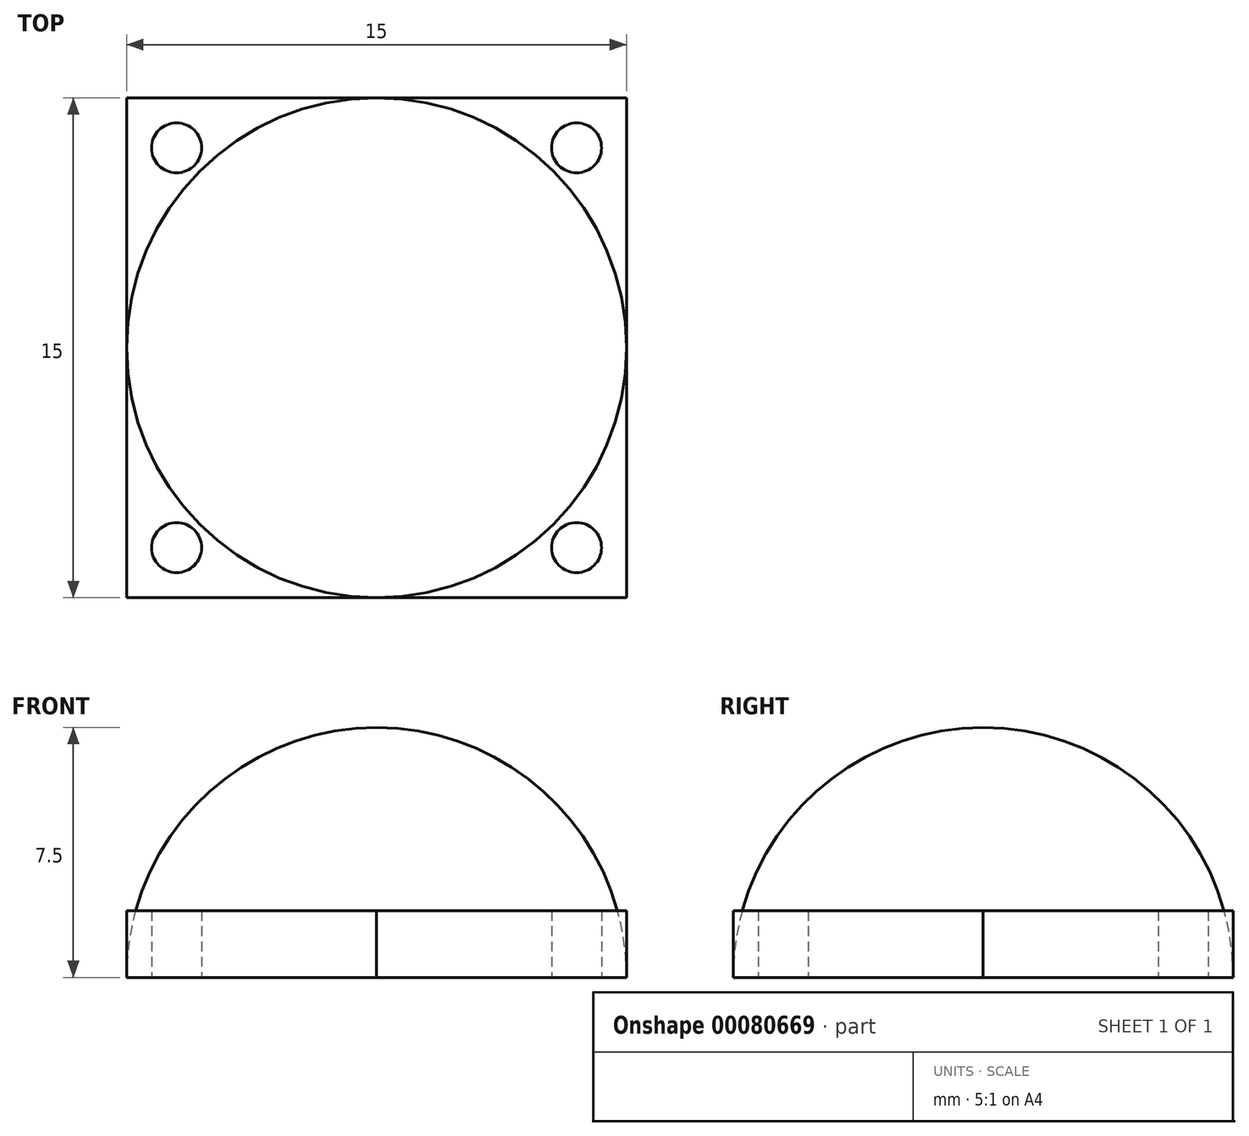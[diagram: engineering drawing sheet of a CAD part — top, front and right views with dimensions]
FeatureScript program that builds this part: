
annotation { "Feature Type Name" : "Feature", "Feature Type Description" : "" }
export const myFeature = defineFeature(function(context is Context, id is Id, definition is map)
    precondition{}
    {
        {
            var Q0;
            Q0=qCreatedBy(makeId("Top.planeOp"),FACE);
            var sketch = newSketch(context, id + "F0", { "sketchPlane" : qUnion([Q0])});
            skLineSegment(sketch, "E0.bottom", {"start": v(7.5, -7.5) * mm, "end": v(-7.5, -7.5) * mm});
            skLineSegment(sketch, "E0.top", {"start": v(7.5, 7.5) * mm, "end": v(-7.5, 7.5) * mm});
            skLineSegment(sketch, "E0.left", {"start": v(7.5, -7.5) * mm, "end": v(7.5, 7.5) * mm});
            skLineSegment(sketch, "E0.right", {"start": v(-7.5, -7.5) * mm, "end": v(-7.5, 7.5) * mm});
            skPoint(sketch, "E0.middle", {"position": v(0, 0) * mm});
            skCircle(sketch, "E1", {"center": v(0, 0) * mm, "radius": 7.5 * mm});
            skLineSegment(sketch, "E2", {"start": v(0, 0) * mm, "end": v(7.5, 0) * mm, "construction": true});
            skLineSegment(sketch, "E3", {"start": v(0, 7.5) * mm, "end": v(0, -7.5) * mm});
            skCircle(sketch, "E4", {"center": v(-6, 6) * mm, "radius": 0.75 * mm});
            skCircle(sketch, "E5.1.0", {"center": v(-6, -6) * mm, "radius": 0.75 * mm});
            skCircle(sketch, "E5.2.0", {"center": v(6, -6) * mm, "radius": 0.75 * mm});
            skCircle(sketch, "E5.3.0", {"center": v(6, 6) * mm, "radius": 0.75 * mm});
            skSolve(sketch);
        }
        {
            var Q0;
            {var subQ0=sQuery(id+"F0.wireOp",EDGE,"E3");Q0=makeQuery(id+"F0.imprint","IMPRINT",FACE,{"disambiguationData":[TD([[makeQuery(id+"F0.imprint","IMPRINT",EDGE,{"derivedFrom":subQ0}),-1.0]])]});}
            var Q1;
            Q1=sQuery(id+"F0.wireOp",EDGE,"E3");
            revolve(context, id + "F1", {"entities" : qUnion([Q0]), "axis" : qUnion([Q1]), "revolveType" : RevolveType.ONE_DIRECTION, "oppositeDirection" : true, "angle" : 180 * degree});
        }
        {
            var Q0;
            {var subQ0=sQuery(id+"F0.wireOp",EDGE,"E0.right");var subQ1=sQuery(id+"F0.wireOp",EDGE,"E0.top");var subQ2=makeQuery(id+"F0.imprint","INTERSECT",VERTEX,{"derivedFrom":[subQ1,subQ0]});Q0=makeQuery(id+"F0.imprint","IMPRINT",FACE,{"disambiguationData":[TD([[makeQuery(id+"F0.imprint","IMPRINT",EDGE,{"disambiguationData":[TD([[subQ2,1.0]])],"derivedFrom":subQ0}),-1.0]])]});}
            var Q1;
            {var subQ0=sQuery(id+"F0.wireOp",EDGE,"E0.right");var subQ1=sQuery(id+"F0.wireOp",EDGE,"E0.bottom");var subQ2=makeQuery(id+"F0.imprint","INTERSECT",VERTEX,{"derivedFrom":[subQ1,subQ0]});Q1=makeQuery(id+"F0.imprint","IMPRINT",FACE,{"disambiguationData":[TD([[makeQuery(id+"F0.imprint","IMPRINT",EDGE,{"disambiguationData":[TD([[subQ2,-1.0]])],"derivedFrom":subQ0}),-1.0]])]});}
            var Q2;
            {var subQ0=sQuery(id+"F0.wireOp",EDGE,"E0.left");var subQ1=sQuery(id+"F0.wireOp",EDGE,"E0.bottom");var subQ2=makeQuery(id+"F0.imprint","INTERSECT",VERTEX,{"derivedFrom":[subQ1,subQ0]});Q2=makeQuery(id+"F0.imprint","IMPRINT",FACE,{"disambiguationData":[TD([[makeQuery(id+"F0.imprint","IMPRINT",EDGE,{"disambiguationData":[TD([[subQ2,-1.0]])],"derivedFrom":subQ0}),1.0]])]});}
            var Q3;
            {var subQ0=sQuery(id+"F0.wireOp",EDGE,"E0.left");var subQ1=sQuery(id+"F0.wireOp",EDGE,"E0.top");var subQ2=makeQuery(id+"F0.imprint","INTERSECT",VERTEX,{"derivedFrom":[subQ1,subQ0]});Q3=makeQuery(id+"F0.imprint","IMPRINT",FACE,{"disambiguationData":[TD([[makeQuery(id+"F0.imprint","IMPRINT",EDGE,{"disambiguationData":[TD([[subQ2,1.0]])],"derivedFrom":subQ0}),1.0]])]});}
            extrude(context, id + "F2", {"entities" : qUnion([Q0, Q1, Q2, Q3]), "operationType" : NewBodyOperationType.ADD, "depth" : 2 * mm});
        }
    });
